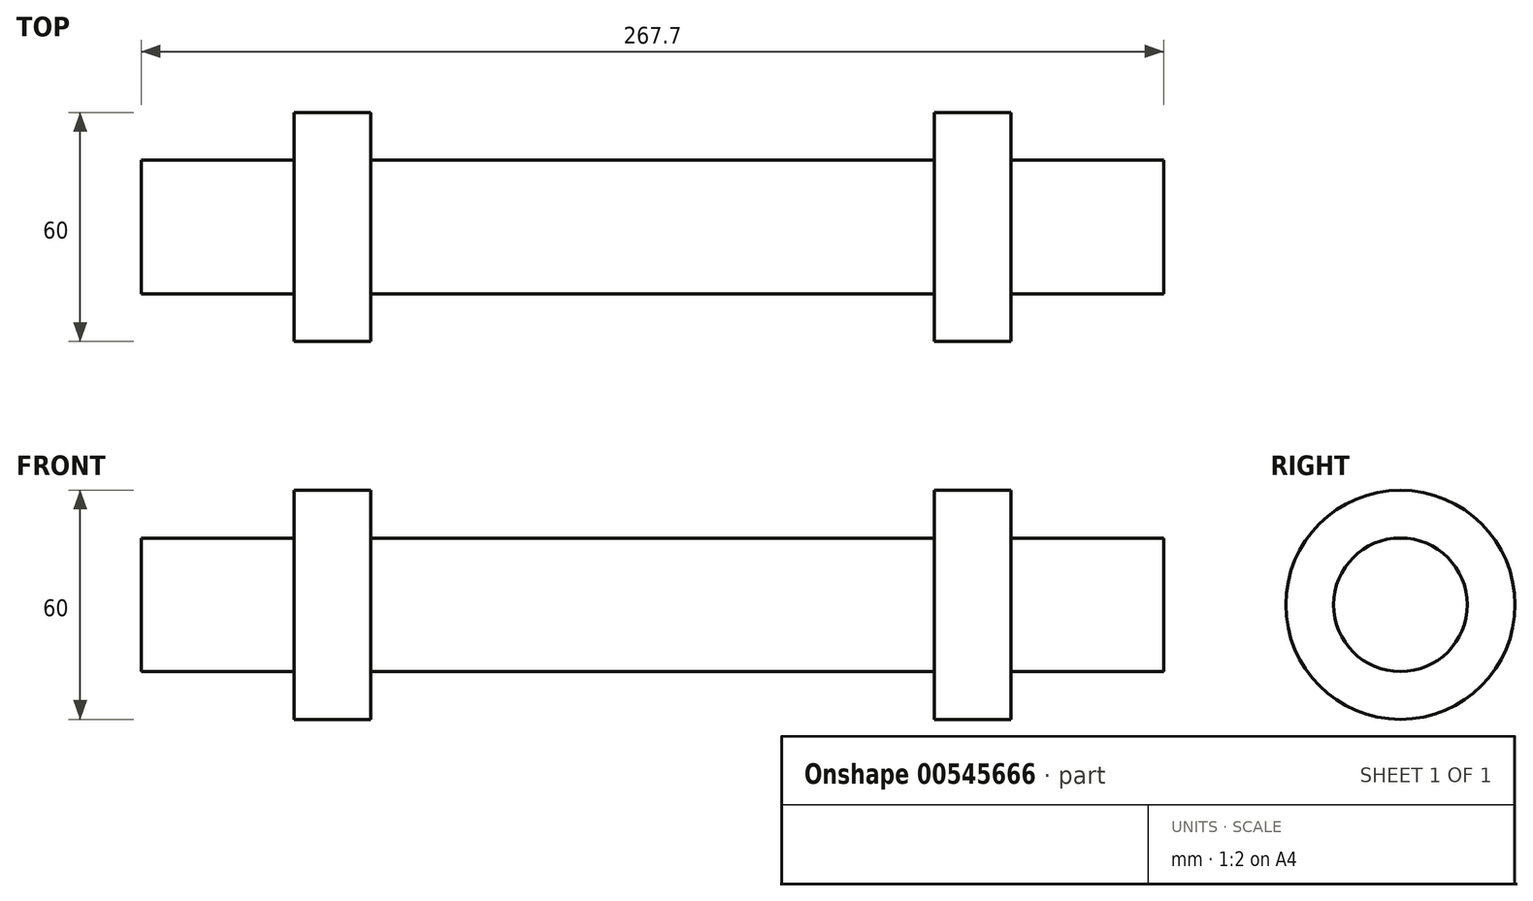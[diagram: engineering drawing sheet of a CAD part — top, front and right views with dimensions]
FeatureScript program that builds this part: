
annotation { "Feature Type Name" : "Feature", "Feature Type Description" : "" }
export const myFeature = defineFeature(function(context is Context, id is Id, definition is map)
    precondition{}
    {
        {
            var Q0;
            Q0=qCreatedBy(makeId("Front.planeOp"),FACE);
            var sketch = newSketch(context, id + "F0", { "sketchPlane" : qUnion([Q0])});
            skLineSegment(sketch, "E0", {"start": v(0, 0) * mm, "end": v(0, 17.5) * mm});
            skLineSegment(sketch, "E1", {"start": v(0, 17.5) * mm, "end": v(73.85, 17.5) * mm});
            skLineSegment(sketch, "E2", {"start": v(73.85, 17.5) * mm, "end": v(73.85, 30) * mm});
            skLineSegment(sketch, "E3", {"start": v(73.85, 30) * mm, "end": v(93.85, 30) * mm});
            skLineSegment(sketch, "E4", {"start": v(93.85, 30) * mm, "end": v(93.85, 17.5) * mm});
            skLineSegment(sketch, "E5", {"start": v(93.85, 17.5) * mm, "end": v(133.85, 17.5) * mm});
            skLineSegment(sketch, "E6", {"start": v(133.85, 17.5) * mm, "end": v(133.85, 0) * mm});
            skLineSegment(sketch, "E7", {"start": v(133.85, 0) * mm, "end": v(0, 0) * mm});
            skSolve(sketch);
        }
        {
            var Q0;
            Q0 = qSketchRegion(id + "F0", true);
            var Q1;
            Q1=sQuery(id+"F0.wireOp",EDGE,"E7");
            revolve(context, id + "F1", {"entities" : qUnion([Q0]), "axis" : qUnion([Q1]), "revolveType" : RevolveType.FULL});
        }
        {
            var Q0;
            Q0=makeQuery(id+"F1.opRevolve","SWEPT_BODY",BODY,{"disambiguationData":[OSD([sQuery(id+"F0.wireOp",EDGE,"E0"),sQuery(id+"F0.wireOp",EDGE,"E1"),sQuery(id+"F0.wireOp",EDGE,"E2"),sQuery(id+"F0.wireOp",EDGE,"E3"),sQuery(id+"F0.wireOp",EDGE,"E4"),sQuery(id+"F0.wireOp",EDGE,"E5"),sQuery(id+"F0.wireOp",EDGE,"E6"),sQuery(id+"F0.wireOp",EDGE,"E7")])]});
            var Q1;
            Q1=makeQuery(id+"F1.opRevolve","SWEPT_FACE",FACE,{"disambiguationData":[OSD([sQuery(id+"F0.wireOp",EDGE,"E0")])]});
            mirror(context, id + "F2", {"operationType" : NewBodyOperationType.ADD, "entities" : qUnion([Q0]), "mirrorPlane" : qUnion([Q1])});
        }
    });
